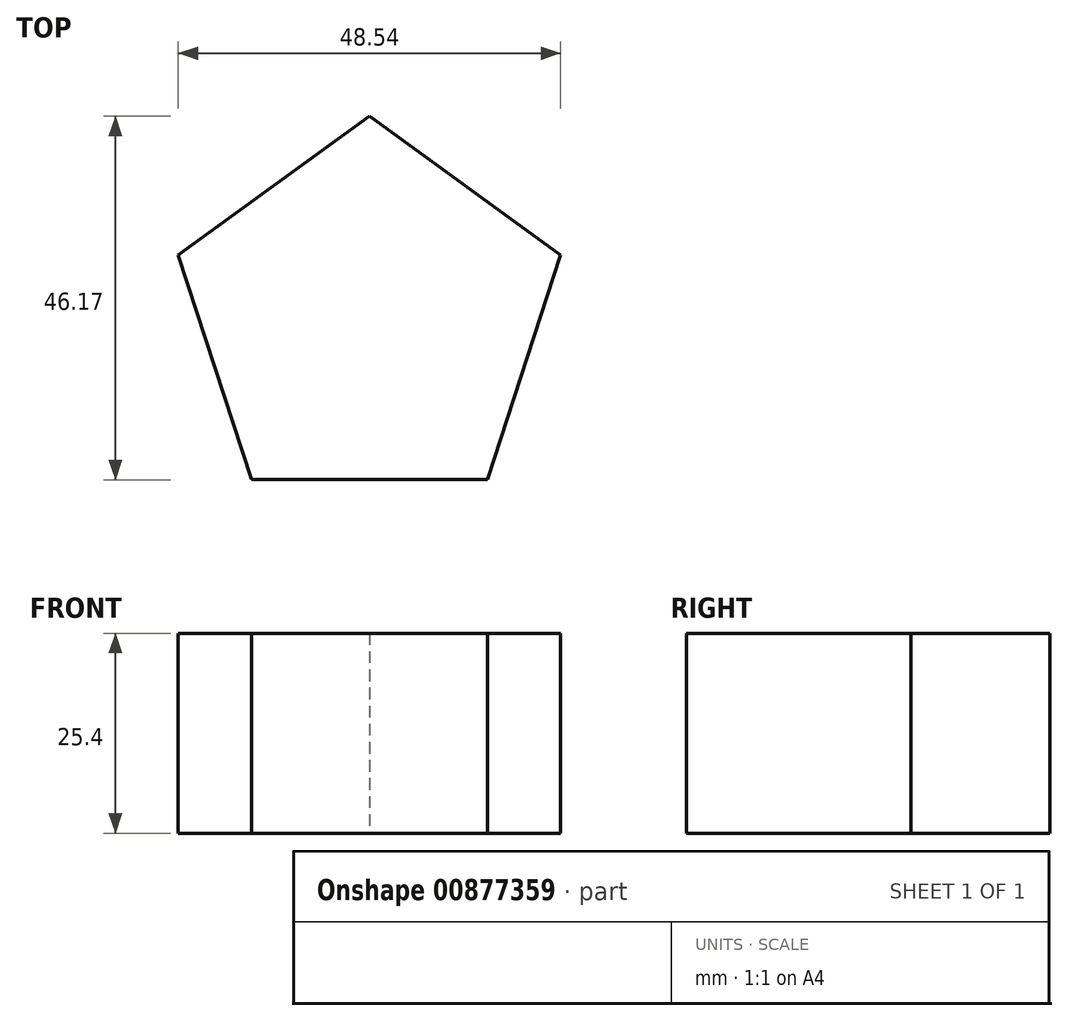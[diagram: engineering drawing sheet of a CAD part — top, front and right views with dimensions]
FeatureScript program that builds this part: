
annotation { "Feature Type Name" : "Feature", "Feature Type Description" : "" }
export const myFeature = defineFeature(function(context is Context, id is Id, definition is map)
    precondition{}
    {
        {
            var Q0;
            Q0=qCreatedBy(makeId("Top.planeOp"),FACE);
            var sketch = newSketch(context, id + "F0", { "sketchPlane" : qUnion([Q0])});
            skCircle(sketch, "E0.cCircle", {"center": v(0, 0) * mm, "radius": 20.65 * mm, "construction": true});
            skLineSegment(sketch, "E0.0", {"start": v(24.27, 7.89) * mm, "end": v(15, -20.65) * mm});
            skLineSegment(sketch, "E0.1", {"start": v(15, -20.65) * mm, "end": v(-15, -20.65) * mm});
            skLineSegment(sketch, "E0.2", {"start": v(-15, -20.65) * mm, "end": v(-24.27, 7.89) * mm});
            skLineSegment(sketch, "E0.3", {"start": v(-24.27, 7.89) * mm, "end": v(0, 25.52) * mm});
            skLineSegment(sketch, "E0.4", {"start": v(0, 25.52) * mm, "end": v(24.27, 7.89) * mm});
            skPoint(sketch, "E0.0.midPoint", {"position": v(19.64, -6.38) * mm});
            skSolve(sketch);
        }
        {
            var Q0;
            Q0 = qSketchRegion(id + "F0", true);
            extrude(context, id + "F1", {"entities" : qUnion([Q0]), "depth" : 25.4 * mm, "offsetDistance" : 25.4 * mm});
        }
    });
